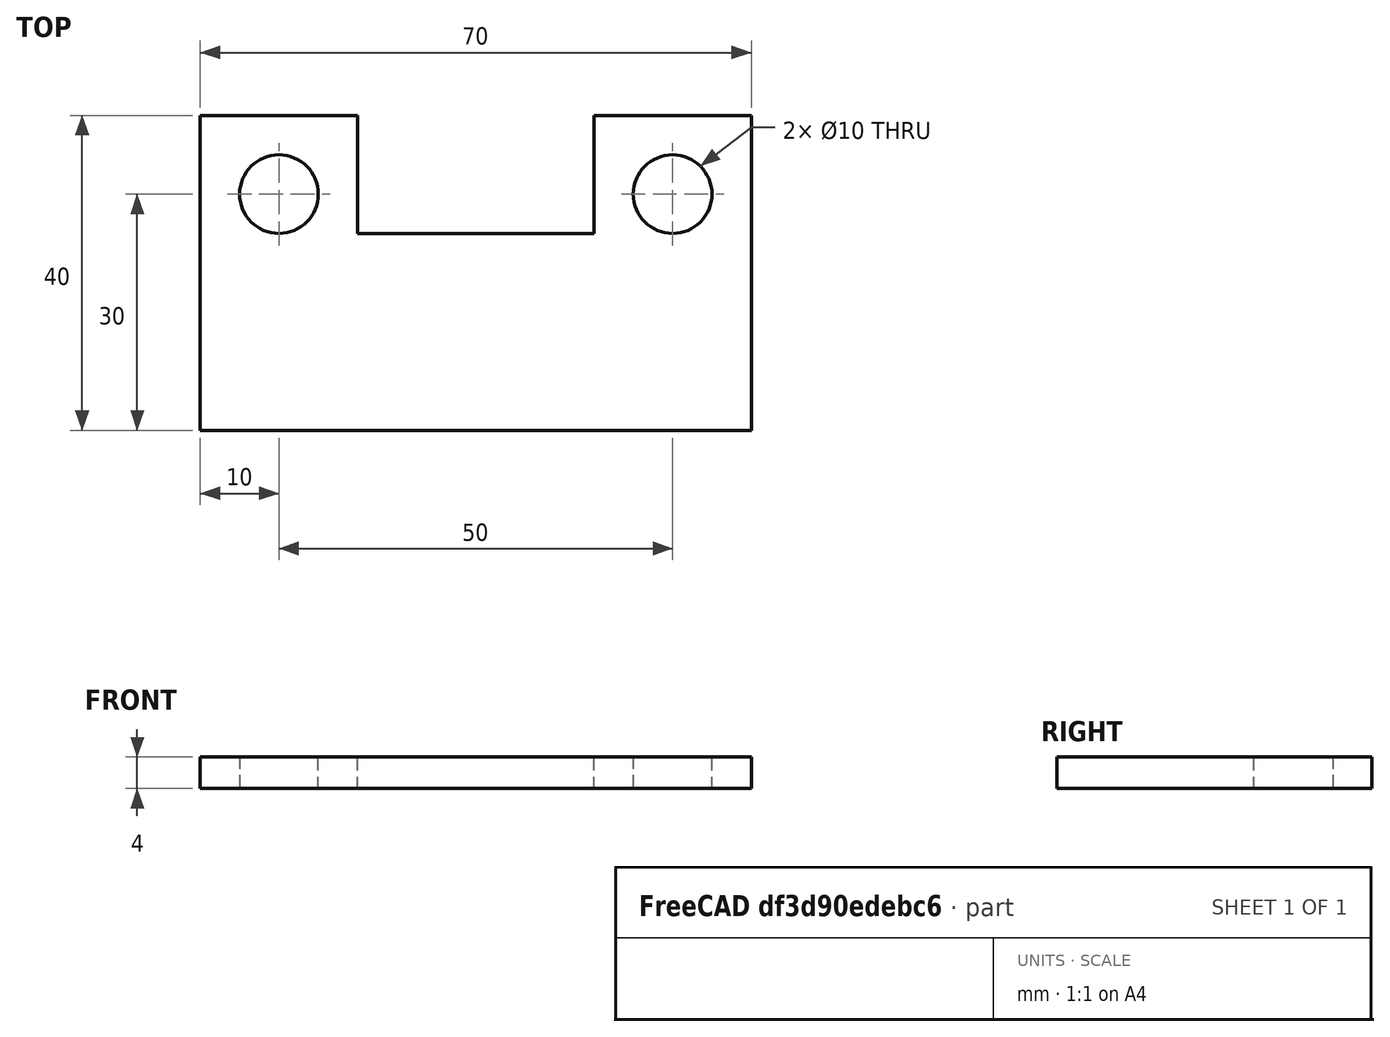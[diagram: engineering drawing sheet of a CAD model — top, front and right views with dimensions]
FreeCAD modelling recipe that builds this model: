
FCSTD DOCUMENT  (FreeCAD 0.21R33771 (Git))
Label: detail_part_workbench
License: All rights reserved
LicenseURL: https://en.wikipedia.org/wiki/All_rights_reserved
objects: Part::Cut×3, Part::Box×2, Part::Cylinder×2
note: 7 computed .brp shape members not serialized (recipe doc carries the construction recipe); baked Part::Feature solids carry a one-line shape summary decoded from their .brp

FEATURE [Part::Box] Box  label="Cube"
  AttacherType = Attacher::AttachEngine3D
  Height = 4
  Length = 70
  Width = 40
FEATURE [Part::Box] Box001  label="Cube001"
  AttacherType = Attacher::AttachEngine3D
  Height = 10
  Length = 30
  Placement = pos=(20,25,0) rot=(0,0,1;0rad)
  Width = 15
FEATURE [Part::Cut] Cut
  Base = -> Box
  Tool = -> Box001
FEATURE [Part::Cylinder] Cylinder
  Angle = 360
  AttacherType = Attacher::AttachEngine3D
  FirstAngle = 0
  Height = 10
  Placement = pos=(10,30,0) rot=(0,0,1;0rad)
  Radius = 5
  SecondAngle = 0
FEATURE [Part::Cut] Cut001
  Base = -> Cut
  Tool = -> Cylinder
FEATURE [Part::Cylinder] Cylinder001
  Angle = 360
  AttacherType = Attacher::AttachEngine3D
  FirstAngle = 0
  Height = 10
  Placement = pos=(60,30,0) rot=(0,0,1;0rad)
  Radius = 5
  SecondAngle = 0
FEATURE [Part::Cut] Cut002
  Base = -> Cut001
  Tool = -> Cylinder001
